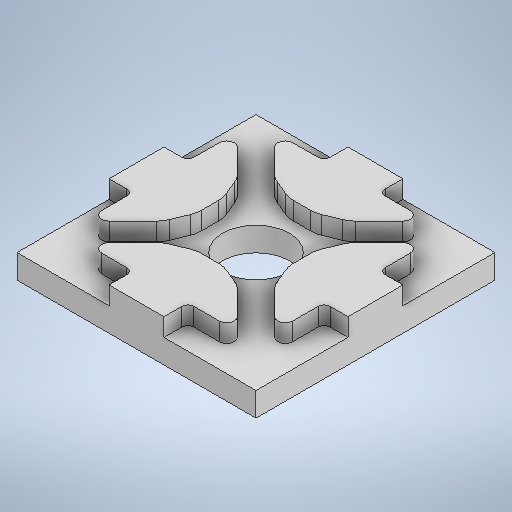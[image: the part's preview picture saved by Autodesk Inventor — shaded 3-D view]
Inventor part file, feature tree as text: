
AUTODESK INVENTOR PART (.ipt)
format: ipt  version: 2025 (Build 290162010, 162A)  size: 388,096 bytes
history: native  units: in
note: dims shown in document units (in); Inventor stores cm internally (conversion verified against a paired STEP export)
features: extrude x2, sketch x2, fillet x1
ambient origin geometry x8: Origin, YZ Plane, XZ Plane, XY Plane, X Axis, Y Axis, Z Axis, Center Point
bodies: Body1 (feature_tree)
feature tree (5):
  extrude  "Extrusion10"  Depth=0.7874in
  extrude  "Extrusion11"  Depth=0.0787in TaperAngle=0.0deg
  fillet  "Rundung3"  Radius=0.1811in
  sketch  "Skizze10"  dims[d78=0.7874in d79=0.7874in]
  sketch  "Skizze11"  dims[d80=0.2205in d81=0.0787in d82=0.0in d83=0.1811in d85=0.0394in d87=0.0498in d89=45.0deg d90=0.0834in d91=45.0deg d92=0.1253in d93=0.0893in d94=0.2421in d95=0.0591in d96=0.0in d97=0.0787in d98=0.1811in d102=45.0deg d104=45.0deg d107=0.2421in d108=0.1811in d112=45.0deg d114=45.0deg d117=0.2421in d118=0.1811in d119=0.0394in d122=45.0deg d124=45.0deg d127=0.2421in d128=0.0591in]
